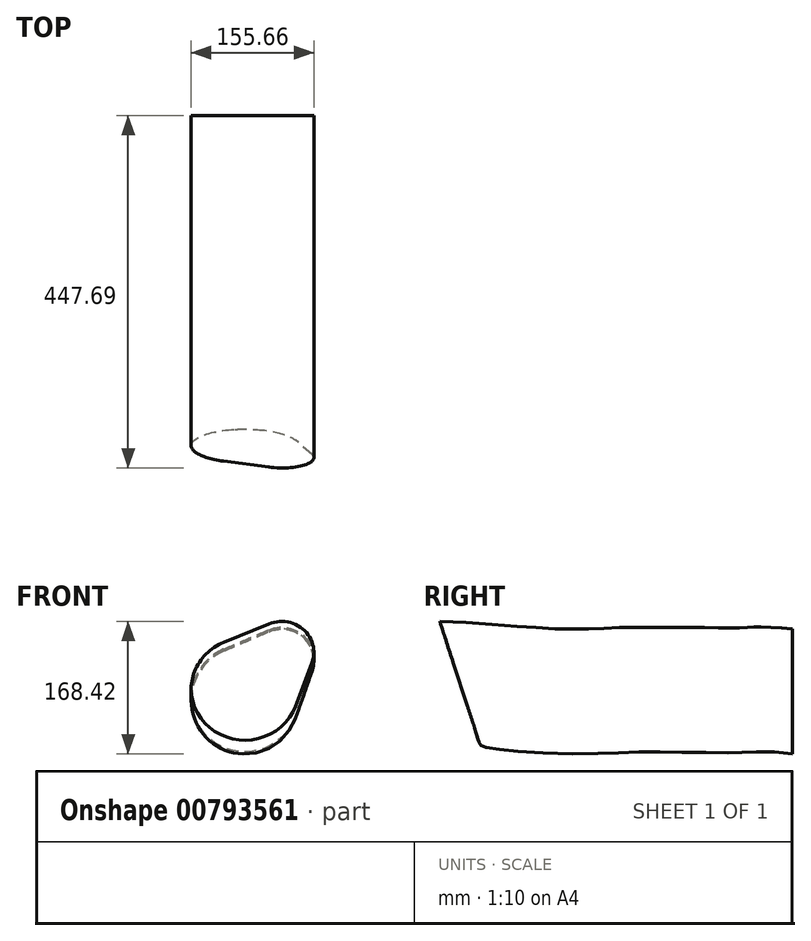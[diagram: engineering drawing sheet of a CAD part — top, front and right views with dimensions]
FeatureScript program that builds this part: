
annotation { "Feature Type Name" : "Feature", "Feature Type Description" : "" }
export const myFeature = defineFeature(function(context is Context, id is Id, definition is map)
    precondition{}
    {
        {
            var Q0;
            Q0=qCreatedBy(makeId("Right.planeOp"),FACE);
            var sketch = newSketch(context, id + "F0", { "sketchPlane" : qUnion([Q0])});
            skLineSegment(sketch, "E0", {"start": v(0, 0) * mm, "end": v(-44.99, 0) * mm});
            skFitSpline(sketch, "E1", {"points": [v(-44.99, 0) * mm, v(-95.71, 0) * mm, v(-123.3, 0) * mm, v(-219.86, 0) * mm, v(-327.65, 0) * mm, v(-462.3, 0) * mm], "startDerivative": vector(-299.96, 11.05) * mm, "endDerivative": vector(-305.05, -87.49) * mm});
            skSolve(sketch);
        }
        {
            var Q0;
            Q0=qCreatedBy(makeId("Front.planeOp"),FACE);
            var sketch = newSketch(context, id + "F1", { "sketchPlane" : qUnion([Q0])});
            skArc(sketch, "E2", {"start": v(-26.88, 62.61) * mm, "mid": v(-46.63, -49.68) * mm, "end": v(64.19, -22.87) * mm});
            skArc(sketch, "E3", {"start": v(85.14, 35.96) * mm, "mid": v(74.61, 79.49) * mm, "end": v(30.5, 87.25) * mm});
            skLineSegment(sketch, "E4", {"start": v(-26.88, 62.61) * mm, "end": v(30.5, 87.25) * mm});
            skLineSegment(sketch, "E5", {"start": v(85.14, 35.96) * mm, "end": v(64.19, -22.87) * mm});
            skSolve(sketch);
        }
        {
            var Q0;
            Q0=makeQuery(id+"F1.imprint","IMPRINT",FACE,{"disambiguationData":[TD([[makeQuery(id+"F1.imprint","IMPRINT",EDGE,{"derivedFrom":sQuery(id+"F1.wireOp",EDGE,"E2")}),1.0]])]});
            var Q1;
            Q1=sQuery(id+"F0.wireOp",EDGE,"E1");
            sweep(context, id + "F2", {"profiles" : qUnion([Q0]), "path" : qUnion([Q1])});
        }
    });
